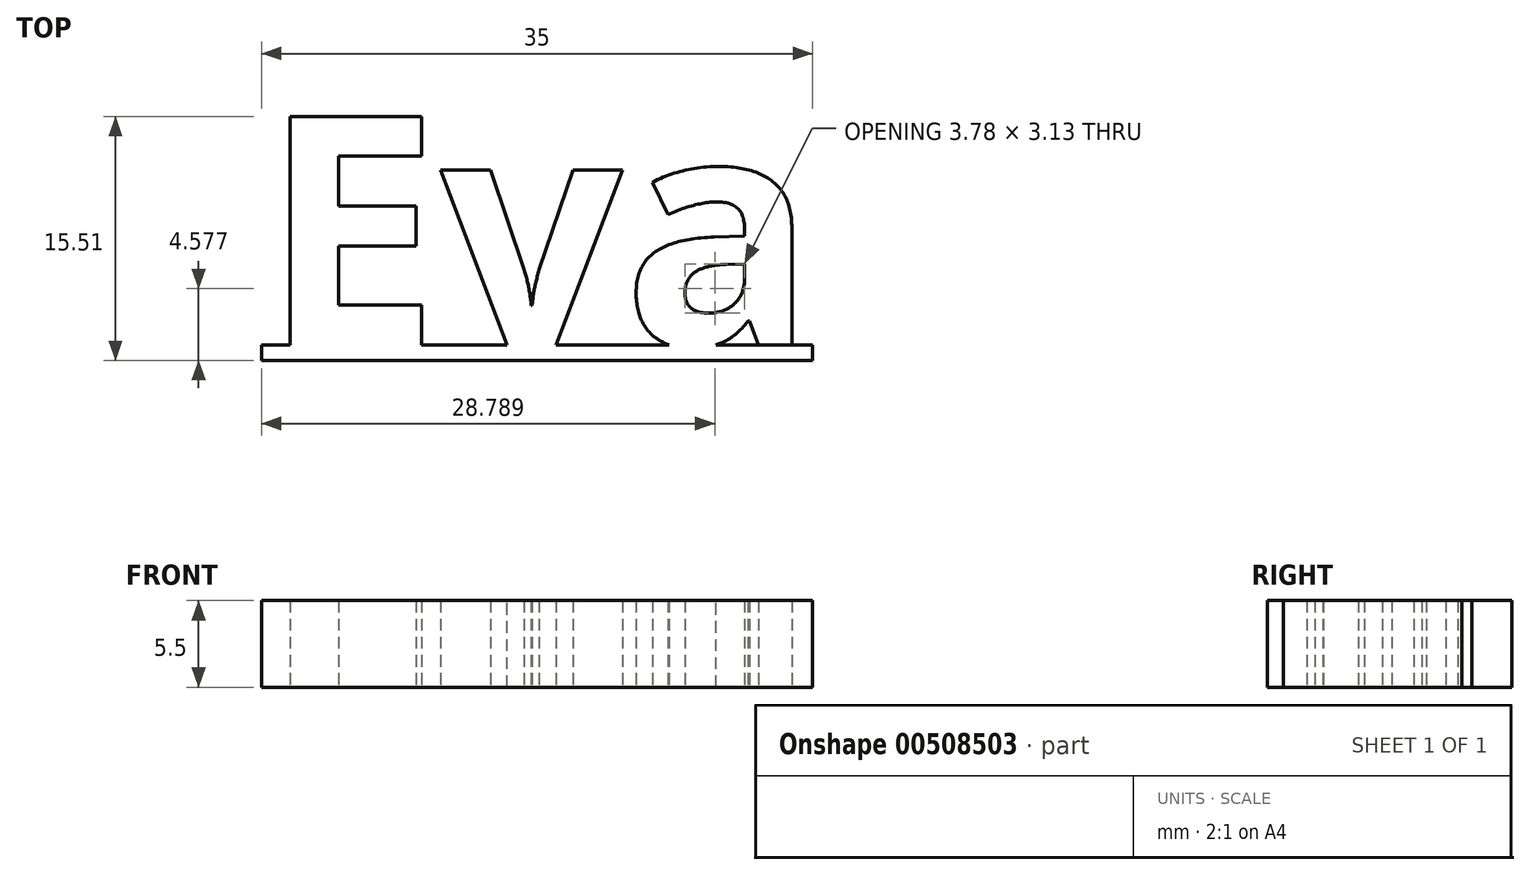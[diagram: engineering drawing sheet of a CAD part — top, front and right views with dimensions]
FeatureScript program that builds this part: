
annotation { "Feature Type Name" : "Feature", "Feature Type Description" : "" }
export const myFeature = defineFeature(function(context is Context, id is Id, definition is map)
    precondition{}
    {
        {
            var Q0;
            Q0=qCreatedBy(makeId("Top.planeOp"),FACE);
            var sketch = newSketch(context, id + "F0", { "sketchPlane" : qUnion([Q0])});
            skText(sketch, "E0", { "text": "Eva", "fontName": "OpenSans-Bold.ttf"});
            skLineSegment(sketch, "E1.bottom", {"start": v(-17.5, -8.8) * mm, "end": v(17.5, -8.8) * mm});
            skLineSegment(sketch, "E1.top", {"start": v(-17.5, -9.8) * mm, "end": v(17.5, -9.8) * mm});
            skLineSegment(sketch, "E1.left", {"start": v(-17.5, -8.8) * mm, "end": v(-17.5, -9.8) * mm});
            skLineSegment(sketch, "E1.right", {"start": v(17.5, -8.8) * mm, "end": v(17.5, -9.8) * mm});
            const initialGuessF0  = {"E0": [-0.0175, -0.0088, 1, 0, 0.01463]};
            skSetInitialGuess(sketch, initialGuessF0);
            skSolve(sketch);
        }
        {
            var Q0;
            Q0 = qSketchRegion(id + "F0", true);
            extrude(context, id + "F1", {"entities" : qUnion([Q0]), "depth" : 5.5 * mm});
        }
        {
            var Q0;
            Q0 = qSketchRegion(id + "F0", true);
            extrude(context, id + "F2", {"entities" : qUnion([Q0]), "operationType" : NewBodyOperationType.ADD, "depth" : 5 * mm});
        }
    });
